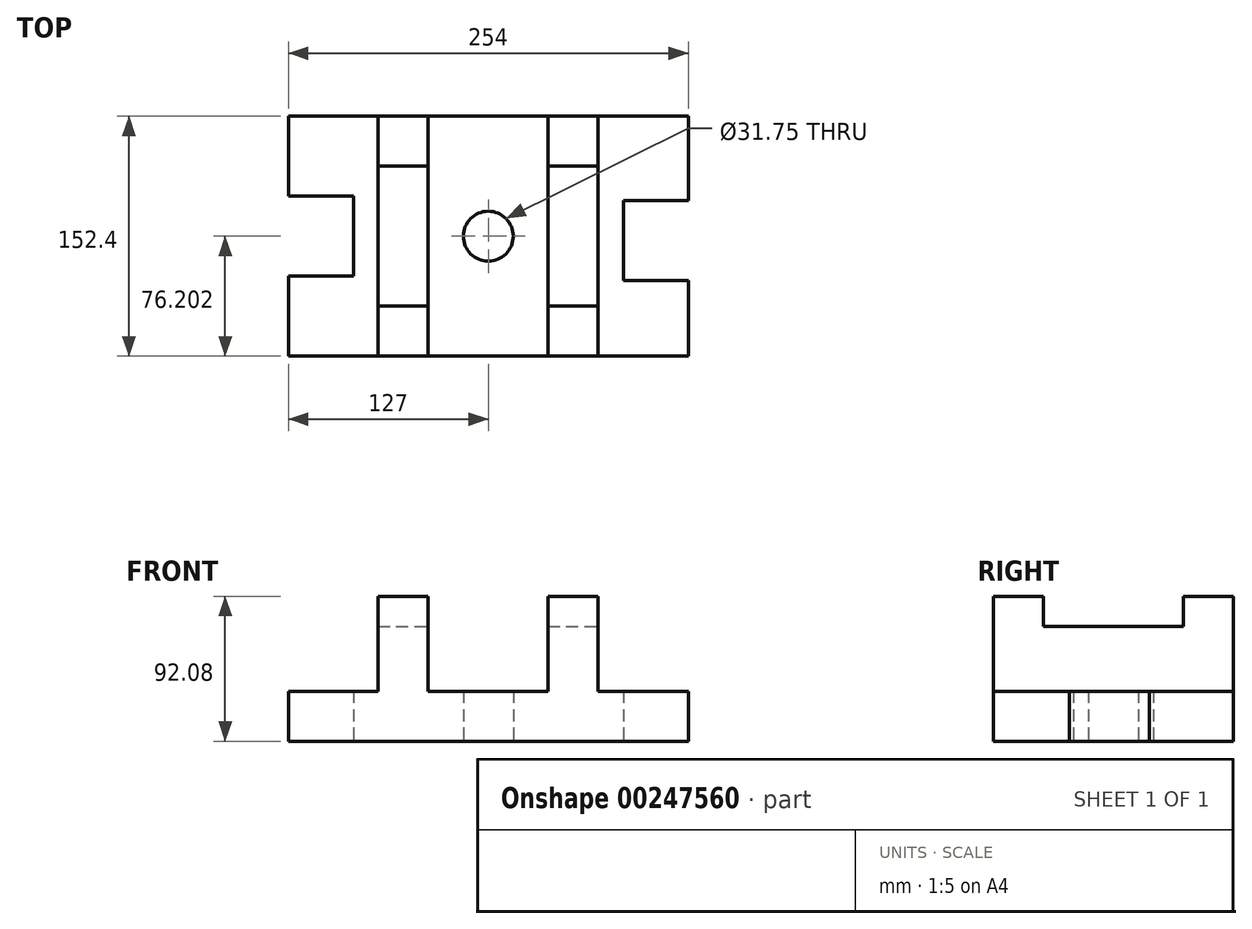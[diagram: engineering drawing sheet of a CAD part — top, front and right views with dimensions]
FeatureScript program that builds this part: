
annotation { "Feature Type Name" : "Feature", "Feature Type Description" : "" }
export const myFeature = defineFeature(function(context is Context, id is Id, definition is map)
    precondition{}
    {
        {
            var Q0;
            Q0=qCreatedBy(makeId("Top.planeOp"),FACE);
            var sketch = newSketch(context, id + "F0", { "sketchPlane" : qUnion([Q0])});
            skLineSegment(sketch, "E0.bottom", {"start": v(-127, 63.52) * mm, "end": v(127, 63.52) * mm});
            skLineSegment(sketch, "E0.top", {"start": v(-127, -88.88) * mm, "end": v(127, -88.88) * mm});
            skLineSegment(sketch, "E0.left", {"start": v(-127, 63.52) * mm, "end": v(-127, -88.88) * mm});
            skLineSegment(sketch, "E0.right", {"start": v(127, 63.52) * mm, "end": v(127, -88.88) * mm});
            skLineSegment(sketch, "E1", {"start": v(127, 10.12) * mm, "end": v(85.72, 10.12) * mm});
            skLineSegment(sketch, "E2", {"start": v(127, -40.68) * mm, "end": v(85.72, -40.68) * mm});
            skLineSegment(sketch, "E3", {"start": v(85.72, 10.12) * mm, "end": v(85.72, -40.68) * mm});
            skLineSegment(sketch, "E4", {"start": v(-127, 12.72) * mm, "end": v(-85.73, 12.72) * mm});
            skLineSegment(sketch, "E5", {"start": v(-127, -38.08) * mm, "end": v(-85.73, -38.08) * mm});
            skLineSegment(sketch, "E6", {"start": v(-85.73, 12.72) * mm, "end": v(-85.73, -38.08) * mm});
            skLineSegment(sketch, "E7", {"start": v(69.77, 63.52) * mm, "end": v(69.77, -88.88) * mm});
            skLineSegment(sketch, "E8", {"start": v(-69.93, 63.52) * mm, "end": v(-69.93, -88.88) * mm});
            skLineSegment(sketch, "E9", {"start": v(-38.18, 63.52) * mm, "end": v(-38.18, -88.88) * mm});
            skLineSegment(sketch, "E10", {"start": v(38.02, 63.52) * mm, "end": v(38.02, -88.88) * mm});
            skLineSegment(sketch, "E11", {"start": v(38.02, 31.77) * mm, "end": v(69.77, 31.77) * mm});
            skLineSegment(sketch, "E12", {"start": v(38.02, -57.13) * mm, "end": v(69.77, -57.13) * mm});
            skLineSegment(sketch, "E13", {"start": v(-69.93, -57.13) * mm, "end": v(-38.18, -57.13) * mm});
            skLineSegment(sketch, "E14", {"start": v(-69.93, 31.77) * mm, "end": v(-38.18, 31.77) * mm});
            skPoint(sketch, "E15.endSnap0", {"position": v(-85.73, -12.68) * mm});
            skCircle(sketch, "E16", {"center": v(0, -12.68) * mm, "radius": 15.88 * mm});
            skSolve(sketch);
        }
        {
            var Q0;
            {var subQ8=sQuery(id+"F0.wireOp",EDGE,"E4");Q0=makeQuery(id+"F0.imprint","IMPRINT",FACE,{"disambiguationData":[TD([[makeQuery(id+"F0.imprint","IMPRINT",EDGE,{"derivedFrom":subQ8}),1.0]])]});}
            var Q1;
            Q1=makeQuery(id+"F0.imprint","IMPRINT",FACE,{"disambiguationData":[TD([[makeQuery(id+"F0.imprint","IMPRINT",EDGE,{"derivedFrom":sQuery(id+"F0.wireOp",EDGE,"E16")}),-1.0]])]});
            var Q2;
            {var subQ6=sQuery(id+"F0.wireOp",EDGE,"E1");Q2=makeQuery(id+"F0.imprint","IMPRINT",FACE,{"disambiguationData":[TD([[makeQuery(id+"F0.imprint","IMPRINT",EDGE,{"derivedFrom":subQ6}),-1.0]])]});}
            extrude(context, id + "F1", {"entities" : qUnion([Q0, Q1, Q2]), "depth" : 31.75 * mm});
        }
        {
            var Q0;
            {var subQ5=sQuery(id+"F0.wireOp",EDGE,"E14");Q0=makeQuery(id+"F0.imprint","IMPRINT",FACE,{"disambiguationData":[TD([[makeQuery(id+"F0.imprint","IMPRINT",EDGE,{"derivedFrom":subQ5}),1.0]])]});}
            var Q1;
            {var subQ5=sQuery(id+"F0.wireOp",EDGE,"E13");Q1=makeQuery(id+"F0.imprint","IMPRINT",FACE,{"disambiguationData":[TD([[makeQuery(id+"F0.imprint","IMPRINT",EDGE,{"derivedFrom":subQ5}),-1.0]])]});}
            var Q2;
            {var subQ5=sQuery(id+"F0.wireOp",EDGE,"E11");Q2=makeQuery(id+"F0.imprint","IMPRINT",FACE,{"disambiguationData":[TD([[makeQuery(id+"F0.imprint","IMPRINT",EDGE,{"derivedFrom":subQ5}),1.0]])]});}
            var Q3;
            {var subQ5=sQuery(id+"F0.wireOp",EDGE,"E12");Q3=makeQuery(id+"F0.imprint","IMPRINT",FACE,{"disambiguationData":[TD([[makeQuery(id+"F0.imprint","IMPRINT",EDGE,{"derivedFrom":subQ5}),-1.0]])]});}
            extrude(context, id + "F2", {"entities" : qUnion([Q0, Q1, Q2, Q3]), "operationType" : NewBodyOperationType.ADD, "depth" : 92.07 * mm});
        }
        {
            var Q0;
            {var subQ0=sQuery(id+"F0.wireOp",EDGE,"E13");Q0=makeQuery(id+"F0.imprint","IMPRINT",FACE,{"disambiguationData":[TD([[makeQuery(id+"F0.imprint","IMPRINT",EDGE,{"derivedFrom":subQ0}),1.0]])]});}
            var Q1;
            {var subQ0=sQuery(id+"F0.wireOp",EDGE,"E11");Q1=makeQuery(id+"F0.imprint","IMPRINT",FACE,{"disambiguationData":[TD([[makeQuery(id+"F0.imprint","IMPRINT",EDGE,{"derivedFrom":subQ0}),-1.0]])]});}
            extrude(context, id + "F3", {"entities" : qUnion([Q0, Q1]), "operationType" : NewBodyOperationType.ADD, "depth" : 73.02 * mm});
        }
    });
